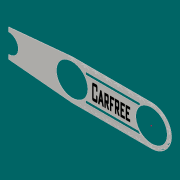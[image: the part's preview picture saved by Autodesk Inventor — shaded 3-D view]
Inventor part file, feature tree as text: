
AUTODESK INVENTOR PART (.ipt)
format: ipt  version: 2016 (Build 200138000, 138)  size: 486,400 bytes
history: native  units: in
note: dims shown in document units (in); Inventor stores cm internally (conversion verified against a paired STEP export)
features: sketch x2, sheet_metal_op x1, other x1
ambient origin geometry x8: Origin, YZ Plane, XZ Plane, XY Plane, X Axis, Y Axis, Z Axis, Center Point
bodies: Body1 (feature_tree)
feature tree (4):
  sheet_metal_op  "Face2"
  sketch  "Sketch2"  dims[d1=8.0in d3=5.0in d4=16.0in d5=1.0in d6=1.0in d7=1.0in d8=0.12in d9=2.3622in d11=180.0deg d13=2.7559in d15=2.8in d16=0.3937in d18=1.0in d21=2.3622in d23=2.7559in d25=0.3937in d26=2.7559in d28=2.8in d29=0.3937in d31=1.0in d33=0.12in]
  sketch  "Sketch1"  dims[d0=8.0in]
  other  "Plate2"
